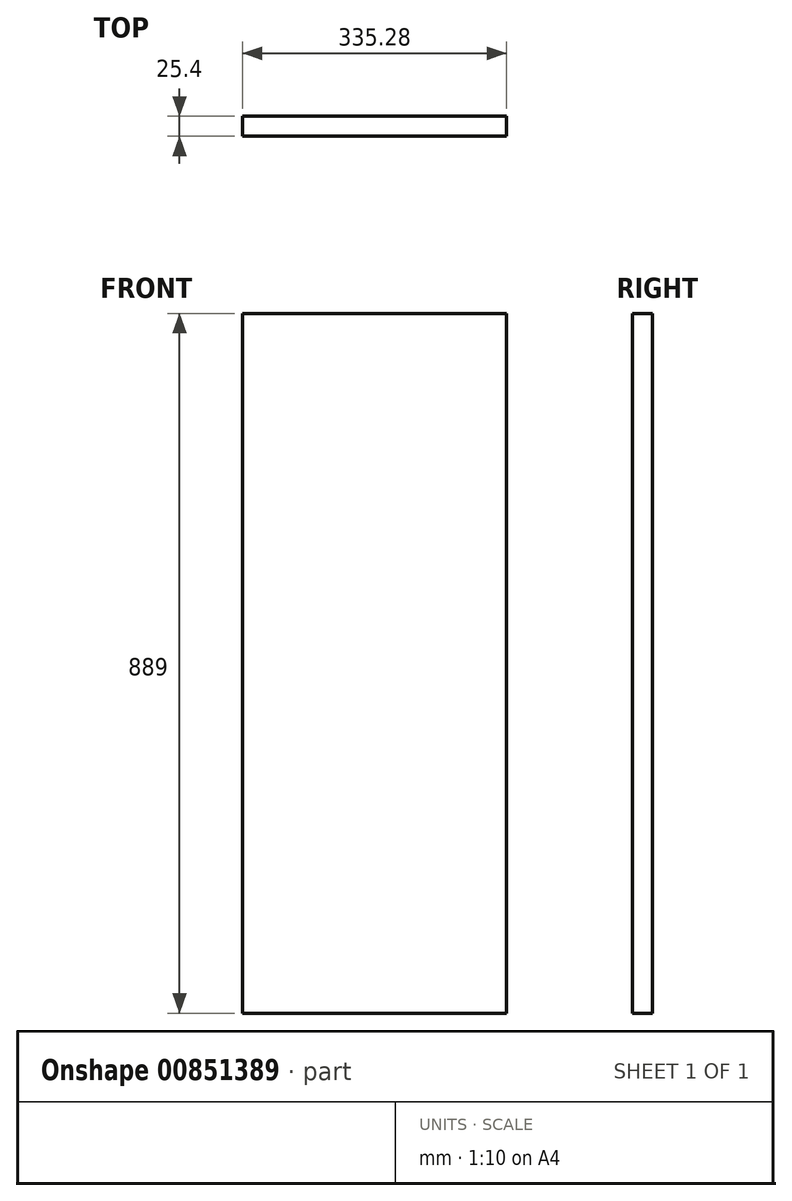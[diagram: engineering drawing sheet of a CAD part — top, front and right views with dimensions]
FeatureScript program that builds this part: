
annotation { "Feature Type Name" : "Feature", "Feature Type Description" : "" }
export const myFeature = defineFeature(function(context is Context, id is Id, definition is map)
    precondition{}
    {
        {
            var Q0;
            Q0=qCreatedBy(makeId("Front.planeOp"),FACE);
            var sketch = newSketch(context, id + "F0", { "sketchPlane" : qUnion([Q0])});
            skLineSegment(sketch, "E0.bottom", {"start": v(-183.57, 683.85) * mm, "end": v(151.71, 683.85) * mm});
            skLineSegment(sketch, "E0.top", {"start": v(-183.57, -205.15) * mm, "end": v(151.71, -205.15) * mm});
            skLineSegment(sketch, "E0.left", {"start": v(-183.57, 683.85) * mm, "end": v(-183.57, -205.15) * mm});
            skLineSegment(sketch, "E0.right", {"start": v(151.71, 683.85) * mm, "end": v(151.71, -205.15) * mm});
            skSolve(sketch);
        }
        {
            var Q0;
            Q0 = qSketchRegion(id + "F0", true);
            extrude(context, id + "F1", {"entities" : qUnion([Q0]), "depth" : 25.4 * mm, "offsetDistance" : 25.4 * mm});
        }
    });
